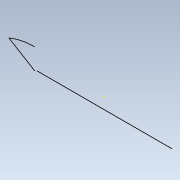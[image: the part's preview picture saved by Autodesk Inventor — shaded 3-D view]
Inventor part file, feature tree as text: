
AUTODESK INVENTOR PART (.ipt)
format: ipt  version: 2021 (Build 250183000, 183)  size: 77,312 bytes
history: native  units: in
note: dims shown in document units (in); Inventor stores cm internally (conversion verified against a paired STEP export)
features: extrude x1, sketch x1
ambient origin geometry x8: Origin, YZ Plane, XZ Plane, XY Plane, X Axis, Y Axis, Z Axis, Center Point
bodies: Solid1 (feature_tree)
feature tree (2):
  extrude  "Extrusion1"  [1 undecoded]
  sketch  "Sketch1"  dims[d0=0.05in d1=0.0in]
note: 1 required parameter value undecoded (feature->parameter linkage not recoverable at this tier; creation-order binding heuristic only, values carry confidence <= 0.55)
